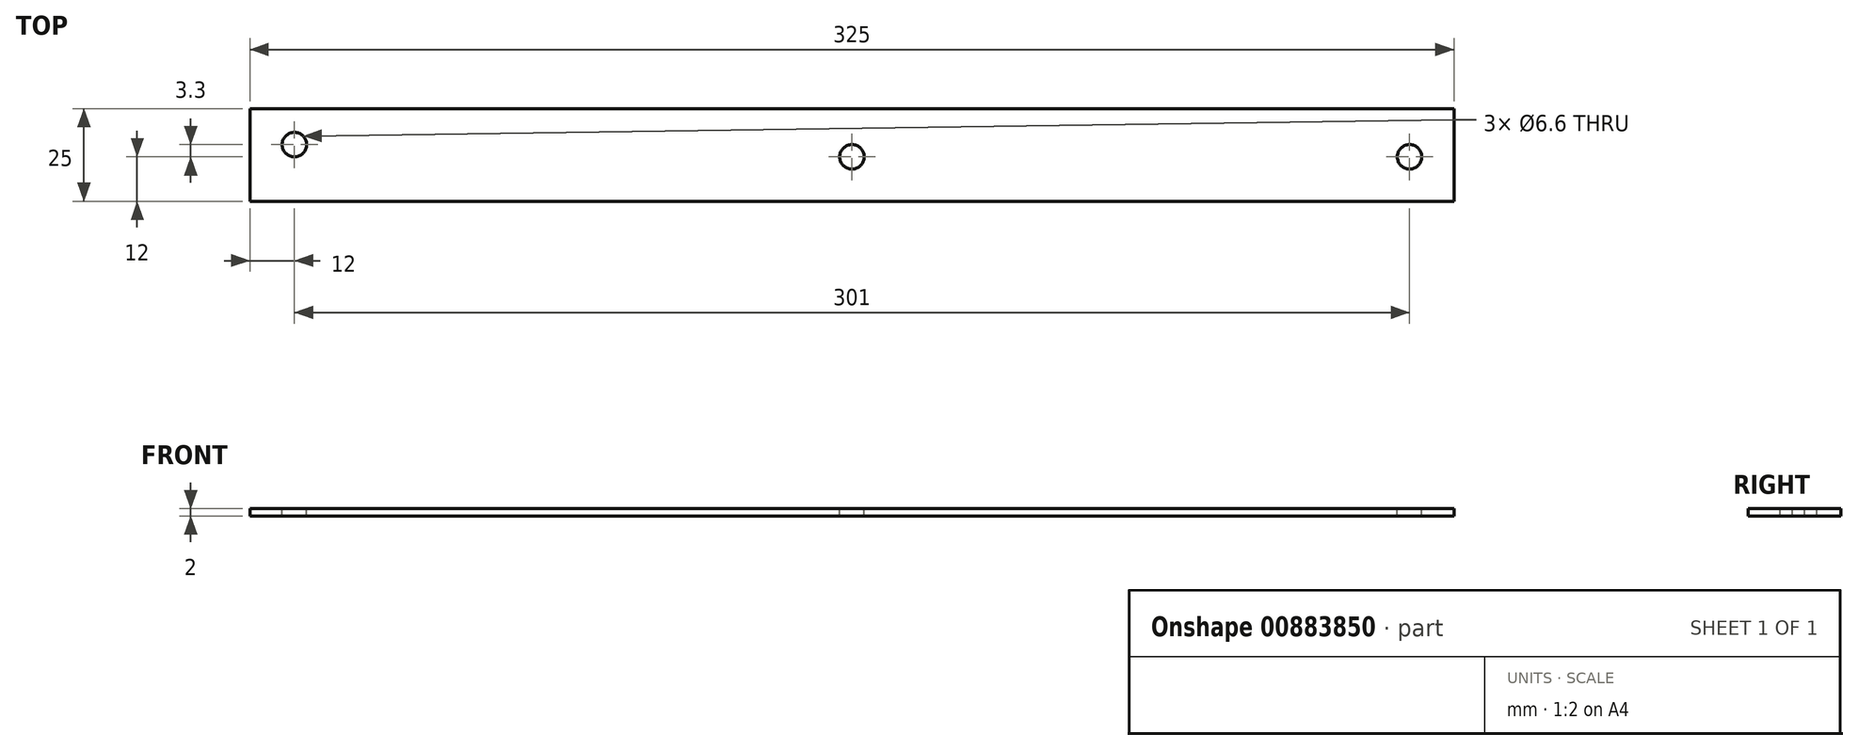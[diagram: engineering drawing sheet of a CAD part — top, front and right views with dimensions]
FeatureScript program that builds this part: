
annotation { "Feature Type Name" : "Feature", "Feature Type Description" : "" }
export const myFeature = defineFeature(function(context is Context, id is Id, definition is map)
    precondition{}
    {
        {
            var Q0;
            Q0=qCreatedBy(makeId("Top.planeOp"),FACE);
            var sketch = newSketch(context, id + "F0", { "sketchPlane" : qUnion([Q0])});
            skLineSegment(sketch, "E0.bottom", {"start": v(0, 0) * mm, "end": v(325, 0) * mm});
            skLineSegment(sketch, "E0.top", {"start": v(0, 25) * mm, "end": v(325, 25) * mm});
            skLineSegment(sketch, "E0.left", {"start": v(0, 0) * mm, "end": v(0, 25) * mm});
            skLineSegment(sketch, "E0.right", {"start": v(325, 0) * mm, "end": v(325, 25) * mm});
            skSolve(sketch);
        }
        {
            var Q0;
            Q0 = qSketchRegion(id + "F0", true);
            extrude(context, id + "F1", {"entities" : qUnion([Q0]), "depth" : 2 * mm, "offsetDistance" : 25 * mm});
        }
        {
            var Q0;
            Q0=makeQuery(id+"F1.opExtrude","CAP_FACE",FACE,{"disambiguationData":[OSD([sQuery(id+"F0.wireOp",EDGE,"E0.bottom"),sQuery(id+"F0.wireOp",EDGE,"E0.top"),sQuery(id+"F0.wireOp",EDGE,"E0.left"),sQuery(id+"F0.wireOp",EDGE,"E0.right")])],"isStart":false});
            var sketch = newSketch(context, id + "F2", { "sketchPlane" : qUnion([Q0])});
            skCircle(sketch, "E1", {"center": v(12, 15.3) * mm, "radius": 3.3 * mm});
            skCircle(sketch, "E2", {"center": v(162.5, 12) * mm, "radius": 3.3 * mm});
            skCircle(sketch, "E3", {"center": v(313, 12) * mm, "radius": 3.3 * mm});
            skPoint(sketch, "E4", {"position": v(0, 12.5) * mm});
            skSolve(sketch);
        }
        {
            var Q0;
            Q0 = qSketchRegion(id + "F2", true);
            extrude(context, id + "F3", {"entities" : qUnion([Q0]), "operationType" : NewBodyOperationType.REMOVE, "oppositeDirection" : true, "depth" : 25 * mm, "offsetDistance" : 25 * mm});
        }
    });
